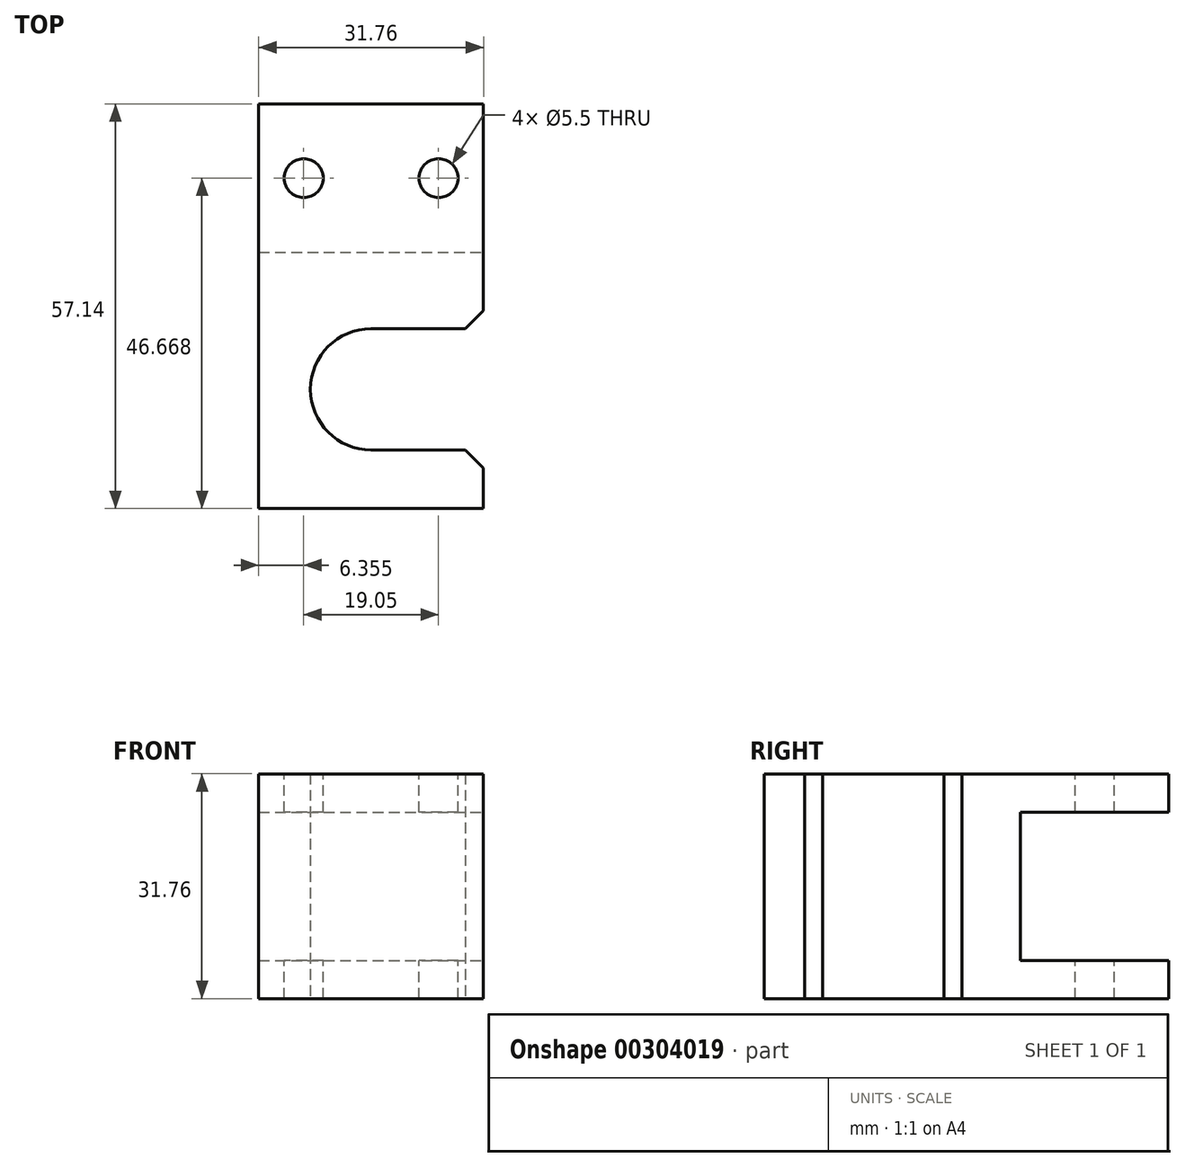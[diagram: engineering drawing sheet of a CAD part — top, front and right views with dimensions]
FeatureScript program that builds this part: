
annotation { "Feature Type Name" : "Feature", "Feature Type Description" : "" }
export const myFeature = defineFeature(function(context is Context, id is Id, definition is map)
    precondition{}
    {
        {
            var Q0;
            Q0=qCreatedBy(makeId("Top.planeOp"),FACE);
            var sketch = newSketch(context, id + "F0", { "sketchPlane" : qUnion([Q0])});
            skLineSegment(sketch, "E0.bottom", {"start": v(15.88, -28.57) * mm, "end": v(-15.88, -28.57) * mm});
            skLineSegment(sketch, "E0.top", {"start": v(15.87, 28.58) * mm, "end": v(-15.88, 28.58) * mm});
            skLineSegment(sketch, "E0.left", {"start": v(15.87, -28.57) * mm, "end": v(15.87, -20.32) * mm});
            skLineSegment(sketch, "E0.right", {"start": v(-15.88, -28.57) * mm, "end": v(-15.88, 28.58) * mm});
            skPoint(sketch, "E0.middle", {"position": v(0, 0) * mm});
            skArc(sketch, "E1", {"start": v(0, -3.17) * mm, "mid": v(-8.57, -11.75) * mm, "end": v(0, -20.32) * mm});
            skLineSegment(sketch, "E2", {"start": v(0, -20.32) * mm, "end": v(15.88, -20.32) * mm});
            skLineSegment(sketch, "E3", {"start": v(0, -3.17) * mm, "end": v(15.88, -3.17) * mm});
            skPoint(sketch, "E3.startSnap0", {"position": v(0, -28.57) * mm});
            skLineSegment(sketch, "E4.trimOffspring", {"start": v(15.88, -3.17) * mm, "end": v(15.88, 28.58) * mm});
            skSolve(sketch);
        }
        {
            var Q0;
            Q0 = qSketchRegion(id + "F0", true);
            extrude(context, id + "F1", {"entities" : qUnion([Q0]), "endBound" : BoundingType.SYMMETRIC, "depth" : 31.75 * mm});
        }
        {
            var Q0;
            Q0=makeQuery(id+"F1.opExtrude","SWEPT_FACE",FACE,{"disambiguationData":[OSD([sQuery(id+"F0.wireOp",EDGE,"E4.trimOffspring")])]});
            var sketch = newSketch(context, id + "F2", { "sketchPlane" : qUnion([Q0])});
            skLineSegment(sketch, "E5.bottom", {"start": v(28.58, 10.48) * mm, "end": v(7.62, 10.48) * mm});
            skLineSegment(sketch, "E5.top", {"start": v(28.58, -10.48) * mm, "end": v(7.62, -10.48) * mm});
            skLineSegment(sketch, "E5.left", {"start": v(28.58, 10.48) * mm, "end": v(28.58, -10.48) * mm});
            skLineSegment(sketch, "E5.right", {"start": v(7.62, 10.48) * mm, "end": v(7.62, -10.48) * mm});
            skLineSegment(sketch, "E6", {"start": v(28.58, 0) * mm, "end": v(7.62, 0) * mm, "construction": true});
            skSolve(sketch);
        }
        {
            var Q0;
            Q0 = qSketchRegion(id + "F2", true);
            extrude(context, id + "F3", {"entities" : qUnion([Q0]), "operationType" : NewBodyOperationType.REMOVE, "endBound" : BoundingType.THROUGH_ALL, "oppositeDirection" : true, "depth" : 25.4 * mm});
        }
        {
            var Q0;
            Q0=makeQuery(id+"F1.opExtrude","CAP_FACE",FACE,{"disambiguationData":[OSD([sQuery(id+"F0.wireOp",EDGE,"E0.bottom"),sQuery(id+"F0.wireOp",EDGE,"E0.top"),sQuery(id+"F0.wireOp",EDGE,"E0.left"),sQuery(id+"F0.wireOp",EDGE,"E0.right"),sQuery(id+"F0.wireOp",EDGE,"E1"),sQuery(id+"F0.wireOp",EDGE,"E2"),sQuery(id+"F0.wireOp",EDGE,"E3"),sQuery(id+"F0.wireOp",EDGE,"E4.trimOffspring")])],"isStart":false});
            var sketch = newSketch(context, id + "F4", { "sketchPlane" : qUnion([Q0])});
            skLineSegment(sketch, "E7", {"start": v(9.53, 18.1) * mm, "end": v(-9.53, 18.1) * mm});
            skLineSegment(sketch, "E8", {"start": v(0, 18.1) * mm, "end": v(0, 28.58) * mm});
            skSolve(sketch);
        }
        {
            var Q0;
            Q0=sQuery(id+"F4.wireOp",VERTEX,"E7.end");
            var Q1;
            Q1=sQuery(id+"F4.wireOp",VERTEX,"E7.start");
            var Q2;
            Q2=makeQuery(id+"F1.opExtrude","SWEPT_BODY",BODY,{"disambiguationData":[OSD([sQuery(id+"F0.wireOp",EDGE,"E0.bottom"),sQuery(id+"F0.wireOp",EDGE,"E0.top"),sQuery(id+"F0.wireOp",EDGE,"E0.left"),sQuery(id+"F0.wireOp",EDGE,"E0.right"),sQuery(id+"F0.wireOp",EDGE,"E1"),sQuery(id+"F0.wireOp",EDGE,"E2"),sQuery(id+"F0.wireOp",EDGE,"E3"),sQuery(id+"F0.wireOp",EDGE,"E4.trimOffspring")])]});
            hole(context, id + "F5", {"style" : HoleStyle.SIMPLE, "endStyle" : HoleEndStyle.THROUGH, "standardTappedOrClearance" : lookupTablePath({ "standard" : "ISO", "fit" : "Normal", "size" : "M5", "type" : "Clearance" }), "standardBlindInLast" : lookupTablePath({ "fit" : "Standard", "standard" : "ISO", "size" : "M5", "type" : "Clearance" }), "holeDiameter" : 5.5 * mm, "tappedDepth" : 12.7 * mm, "tapClearance" : 3, "startFromSketch" : true, "locations" : qUnion([Q0, Q1]), "scope" : qUnion([Q2])});
        }
        {
            var Q0;
            Q0=makeQuery(id+"F1.opExtrude","SWEPT_EDGE",EDGE,{"disambiguationData":[OSD([sQuery(id+"F0.wireOp",EDGE,"E0.left"),sQuery(id+"F0.wireOp",EDGE,"E2")])]});
            var Q1;
            Q1=makeQuery(id+"F1.opExtrude","SWEPT_EDGE",EDGE,{"disambiguationData":[OSD([sQuery(id+"F0.wireOp",EDGE,"E3"),sQuery(id+"F0.wireOp",EDGE,"E4.trimOffspring")])]});
            chamfer(context, id + "F6", {"entities" : qUnion([Q0, Q1]), "width" : 2.54 * mm, "tangentPropagation" : true});
        }
    });
